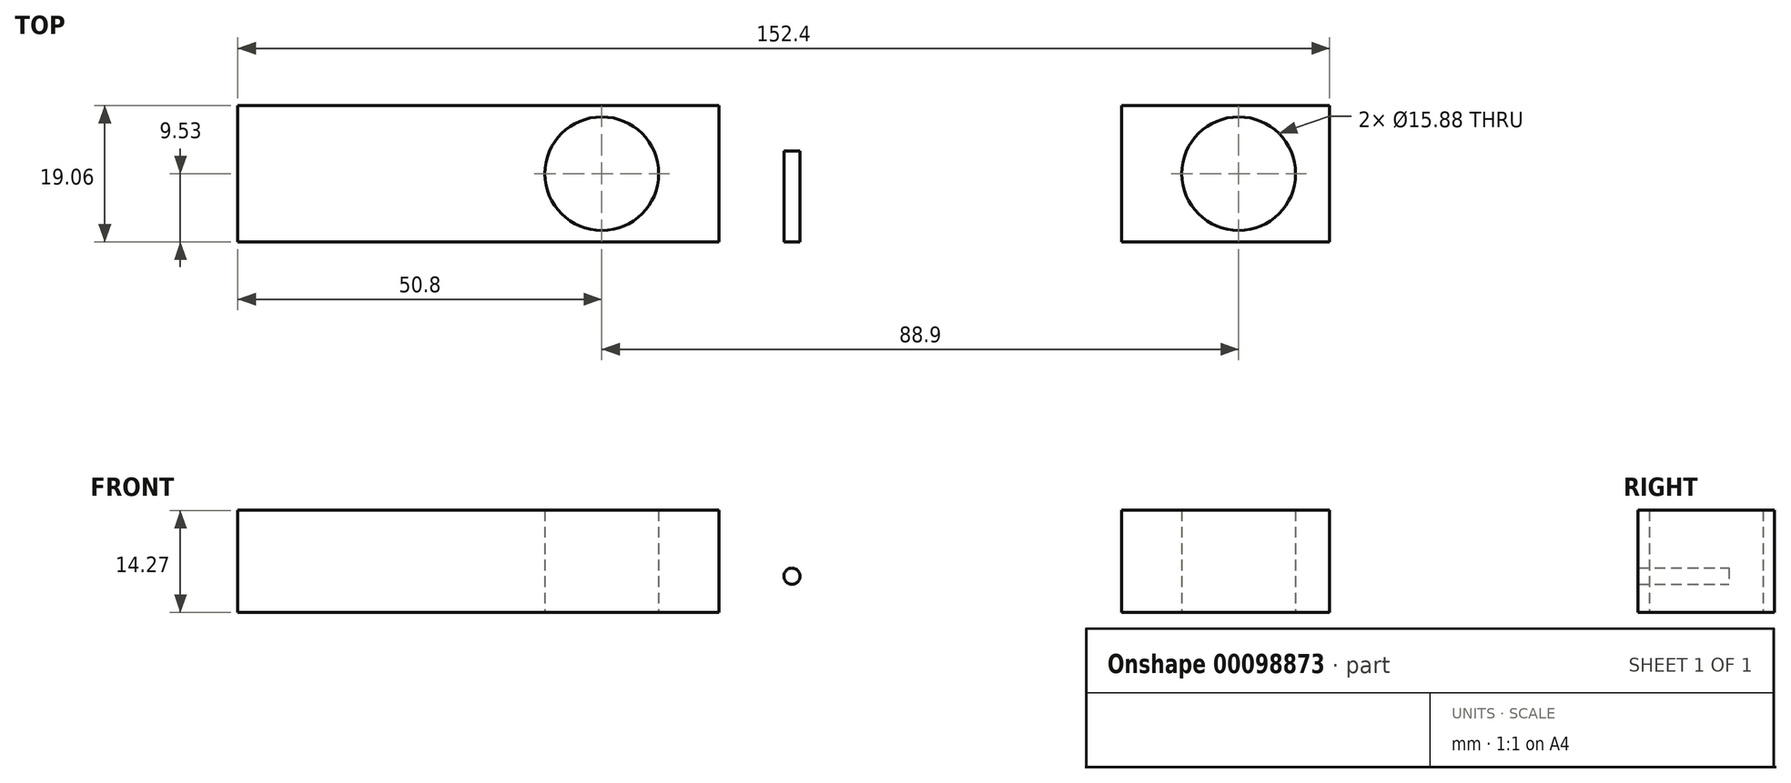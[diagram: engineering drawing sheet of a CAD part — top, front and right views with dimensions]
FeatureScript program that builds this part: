
annotation { "Feature Type Name" : "Feature", "Feature Type Description" : "" }
export const myFeature = defineFeature(function(context is Context, id is Id, definition is map)
    precondition{}
    {
        {
            var Q0;
            Q0=qCreatedBy(makeId("Top.planeOp"),FACE);
            var sketch = newSketch(context, id + "F0", { "sketchPlane" : qUnion([Q0])});
            skLineSegment(sketch, "E0.bottom", {"start": v(57.15, 9.53) * mm, "end": v(28.1, 9.53) * mm});
            skLineSegment(sketch, "E0.top", {"start": v(57.15, -9.53) * mm, "end": v(-95.25, -9.53) * mm});
            skLineSegment(sketch, "E0.right", {"start": v(-95.25, 9.52) * mm, "end": v(-95.25, -9.53) * mm});
            skPoint(sketch, "E0.middle", {"position": v(0, 0) * mm});
            skCircle(sketch, "E1", {"center": v(-44.45, 0) * mm, "radius": 7.94 * mm});
            skCircle(sketch, "E2.MirrorC", {"center": v(44.45, 0) * mm, "radius": 7.94 * mm});
            skLineSegment(sketch, "E3", {"start": v(-28.1, 9.53) * mm, "end": v(-28.1, 3.17) * mm});
            skLineSegment(sketch, "E4.MirrorCS", {"start": v(28.1, 9.53) * mm, "end": v(28.1, 3.17) * mm});
            skLineSegment(sketch, "E5", {"start": v(-28.1, 3.17) * mm, "end": v(28.1, 3.18) * mm});
            skLineSegment(sketch, "E6.trimOffspring", {"start": v(-28.1, 9.53) * mm, "end": v(-95.25, 9.53) * mm});
            skLineSegment(sketch, "E7", {"start": v(57.15, 9.53) * mm, "end": v(57.15, -9.53) * mm});
            skPoint(sketch, "E0.left.start.orphan", {"position": v(95.25, 9.52) * mm});
            skPoint(sketch, "E8.orphan", {"position": v(95.25, -9.53) * mm});
            skSolve(sketch);
        }
        {
            var Q0;
            Q0=makeQuery(id+"F0.imprint","IMPRINT",FACE,{"disambiguationData":[TD([[makeQuery(id+"F0.imprint","IMPRINT",EDGE,{"derivedFrom":sQuery(id+"F0.wireOp",EDGE,"E0.bottom")}),1.0]])]});
            extrude(context, id + "F1", {"entities" : qUnion([Q0]), "depth" : 14.27 * mm});
        }
        {
            var Q0;
            Q0=makeQuery(id+"F1.opExtrude","SWEPT_FACE",FACE,{"disambiguationData":[OSD([sQuery(id+"F0.wireOp",EDGE,"E5")])]});
            var sketch = newSketch(context, id + "F2", { "sketchPlane" : qUnion([Q0])});
            skCircle(sketch, "E9", {"center": v(-17.9, 5.08) * mm, "radius": 1.13 * mm});
            skCircle(sketch, "E10.MirrorC", {"center": v(17.9, 5.08) * mm, "radius": 1.13 * mm});
            skSolve(sketch);
        }
        {
            var Q0;
            Q0=makeQuery(id+"F2.imprint","IMPRINT",FACE,{"disambiguationData":[TD([[makeQuery(id+"F2.imprint","IMPRINT",EDGE,{"derivedFrom":sQuery(id+"F2.wireOp",EDGE,"E9")}),1.0]])]});
            var Q1;
            Q1=makeQuery(id+"F2.imprint","IMPRINT",FACE,{"disambiguationData":[TD([[makeQuery(id+"F2.imprint","IMPRINT",EDGE,{"derivedFrom":sQuery(id+"F2.wireOp",EDGE,"E10.MirrorC")}),-1.0]])]});
            extrude(context, id + "F3", {"entities" : qUnion([Q0, Q1]), "operationType" : NewBodyOperationType.REMOVE, "endBound" : BoundingType.THROUGH_ALL, "oppositeDirection" : true, "depth" : 25.4 * mm});
        }
    });
